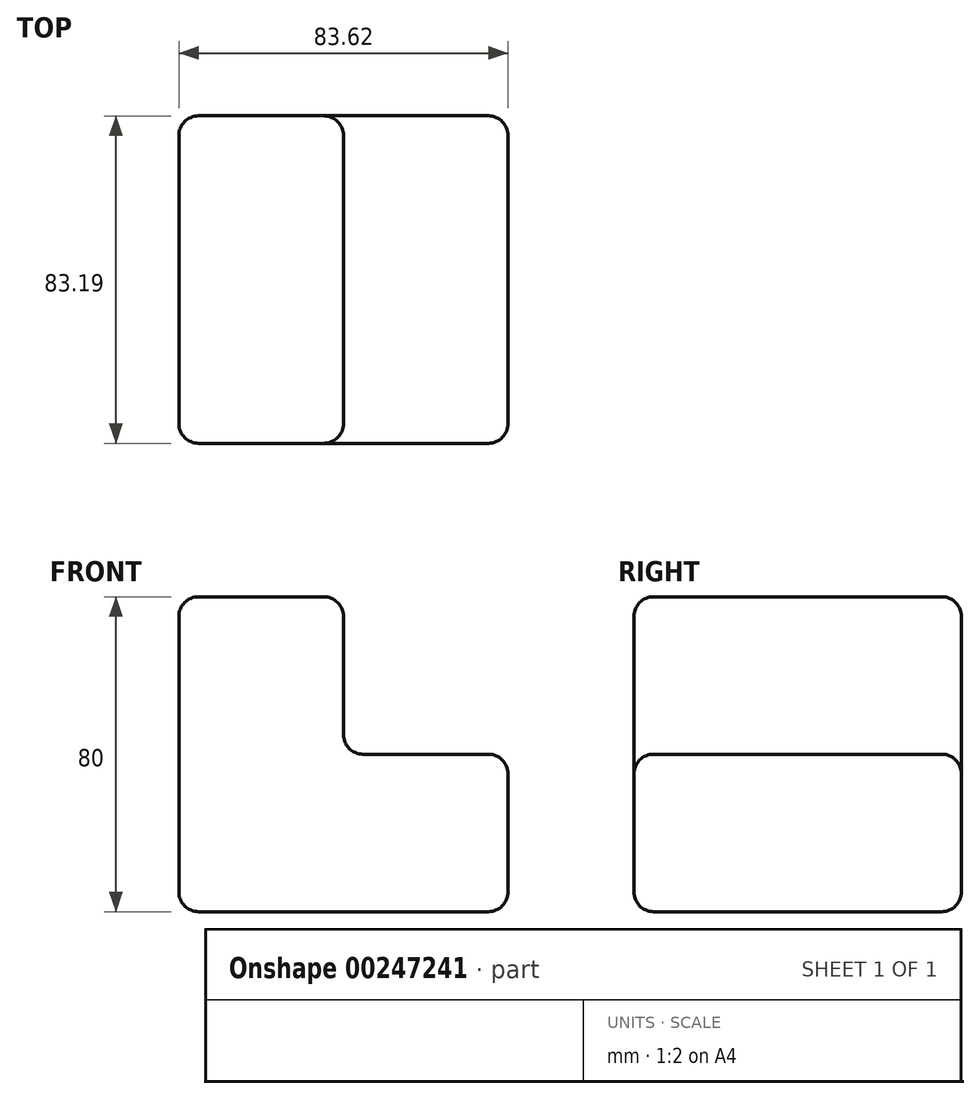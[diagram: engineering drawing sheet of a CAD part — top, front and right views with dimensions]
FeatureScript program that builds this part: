
annotation { "Feature Type Name" : "Feature", "Feature Type Description" : "" }
export const myFeature = defineFeature(function(context is Context, id is Id, definition is map)
    precondition{}
    {
        {
            var Q0;
            Q0=qCreatedBy(makeId("Top.planeOp"),FACE);
            var sketch = newSketch(context, id + "F0", { "sketchPlane" : qUnion([Q0])});
            skLineSegment(sketch, "E0.bottom", {"start": v(-59.13, -45.93) * mm, "end": v(24.5, -45.93) * mm});
            skLineSegment(sketch, "E0.top", {"start": v(-59.13, 37.26) * mm, "end": v(24.5, 37.26) * mm});
            skLineSegment(sketch, "E0.left", {"start": v(-59.13, -45.93) * mm, "end": v(-59.13, 37.26) * mm});
            skLineSegment(sketch, "E0.right", {"start": v(24.5, -45.93) * mm, "end": v(24.5, 37.26) * mm});
            skSolve(sketch);
        }
        {
            var Q0;
            Q0=makeQuery(id+"F0.imprint","IMPRINT",FACE,{"disambiguationData":[TD([[makeQuery(id+"F0.imprint","IMPRINT",EDGE,{"derivedFrom":sQuery(id+"F0.wireOp",EDGE,"E0.bottom")}),1.0]])]});
            extrude(context, id + "F1", {"entities" : qUnion([Q0]), "depth" : 40 * mm});
        }
        {
            var Q0;
            Q0=makeQuery(id+"F1.opExtrude","CAP_FACE",FACE,{"disambiguationData":[OSD([sQuery(id+"F0.wireOp",EDGE,"E0.bottom"),sQuery(id+"F0.wireOp",EDGE,"E0.top"),sQuery(id+"F0.wireOp",EDGE,"E0.left"),sQuery(id+"F0.wireOp",EDGE,"E0.right")])],"isStart":false});
            var sketch = newSketch(context, id + "F2", { "sketchPlane" : qUnion([Q0])});
            skLineSegment(sketch, "E1", {"start": v(-17.32, 37.26) * mm, "end": v(-17.32, -45.93) * mm});
            skSolve(sketch);
        }
        {
            var Q0;
            {var subQ1=sQuery(id+"F2.wireOp",EDGE,"E1");Q0=makeQuery(id+"F2.imprint","IMPRINT",FACE,{"disambiguationData":[TD([[makeQuery(id+"F2.imprint","IMPRINT",EDGE,{"derivedFrom":subQ1}),-1.0]])]});}
            extrude(context, id + "F3", {"entities" : qUnion([Q0]), "operationType" : NewBodyOperationType.ADD, "depth" : 40 * mm});
        }
        {
            var Q0;
            Q0=makeQuery(id+"F3.opExtrude","CAP_EDGE",EDGE,{"disambiguationData":[OSD([sQuery(id+"F2.wireOp",EDGE,"E1")])],"isStart":true});
            var Q1;
            {var subQ0=sQuery(id+"F0.wireOp",EDGE,"E0.left");Q1=makeQuery(id+"F3.boolean.opBoolean","MERGE",FACE,{"derivedFrom":[makeQuery(id+"F1.opExtrude","SWEPT_FACE",FACE,{"disambiguationData":[OSD([subQ0])]}),makeQuery(id+"F3.opExtrude","SWEPT_FACE",FACE,{"disambiguationData":[OSD([subQ0])]})]});}
            var Q2;
            Q2=makeQuery(id+"F1.opExtrude","CAP_EDGE",EDGE,{"disambiguationData":[OSD([sQuery(id+"F0.wireOp",EDGE,"E0.top")])],"isStart":false});
            var Q3;
            Q3=makeQuery(id+"F1.opExtrude","CAP_EDGE",EDGE,{"disambiguationData":[OSD([sQuery(id+"F0.wireOp",EDGE,"E0.bottom")])],"isStart":false});
            var Q4;
            {var subQ0=sQuery(id+"F0.wireOp",EDGE,"E0.top");Q4=makeQuery(id+"F3.boolean.opBoolean","MERGE",FACE,{"derivedFrom":[makeQuery(id+"F1.opExtrude","SWEPT_FACE",FACE,{"disambiguationData":[OSD([subQ0])]}),makeQuery(id+"F3.opExtrude","SWEPT_FACE",FACE,{"disambiguationData":[OSD([subQ0])]})]});}
            var Q5;
            Q5=makeQuery(id+"F3.opExtrude","CAP_EDGE",EDGE,{"disambiguationData":[OSD([sQuery(id+"F0.wireOp",EDGE,"E0.top")])],"isStart":false});
            var Q6;
            Q6=makeQuery(id+"F3.opExtrude","SWEPT_EDGE",EDGE,{"disambiguationData":[OSD([sQuery(id+"F0.wireOp",EDGE,"E0.bottom"),sQuery(id+"F2.wireOp",EDGE,"E1")])]});
            var Q7;
            Q7=makeQuery(id+"F1.opExtrude","CAP_FACE",FACE,{"disambiguationData":[OSD([sQuery(id+"F0.wireOp",EDGE,"E0.bottom"),sQuery(id+"F0.wireOp",EDGE,"E0.top"),sQuery(id+"F0.wireOp",EDGE,"E0.left"),sQuery(id+"F0.wireOp",EDGE,"E0.right")])],"isStart":true});
            var Q8;
            Q8=makeQuery(id+"F1.opExtrude","CAP_EDGE",EDGE,{"disambiguationData":[OSD([sQuery(id+"F0.wireOp",EDGE,"E0.right")])],"isStart":true});
            var Q9;
            Q9=makeQuery(id+"F1.opExtrude","CAP_EDGE",EDGE,{"disambiguationData":[OSD([sQuery(id+"F0.wireOp",EDGE,"E0.right")])],"isStart":false});
            var Q10;
            {var subQ0=sQuery(id+"F0.wireOp",EDGE,"E0.left");var subQ1=sQuery(id+"F0.wireOp",EDGE,"E0.bottom");Q10=makeQuery(id+"F3.boolean.opBoolean","MERGE",EDGE,{"derivedFrom":[makeQuery(id+"F1.opExtrude","SWEPT_EDGE",EDGE,{"disambiguationData":[OSD([subQ1,subQ0])]}),makeQuery(id+"F3.opExtrude","SWEPT_EDGE",EDGE,{"disambiguationData":[OSD([subQ1,subQ0])]})]});}
            var Q11;
            Q11=makeQuery(id+"F3.opExtrude","CAP_FACE",FACE,{"disambiguationData":[OSD([sQuery(id+"F0.wireOp",EDGE,"E0.bottom"),sQuery(id+"F0.wireOp",EDGE,"E0.top"),sQuery(id+"F0.wireOp",EDGE,"E0.left"),sQuery(id+"F2.wireOp",EDGE,"E1")])],"isStart":false});
            var Q12;
            Q12=makeQuery(id+"F3.opExtrude","SWEPT_FACE",FACE,{"disambiguationData":[OSD([sQuery(id+"F2.wireOp",EDGE,"E1")])]});
            var Q13;
            Q13=makeQuery(id+"F1.opExtrude","CAP_EDGE",EDGE,{"disambiguationData":[OSD([sQuery(id+"F0.wireOp",EDGE,"E0.bottom")])],"isStart":true});
            var Q14;
            Q14=makeQuery(id+"F1.opExtrude","SWEPT_FACE",FACE,{"disambiguationData":[OSD([sQuery(id+"F0.wireOp",EDGE,"E0.right")])]});
            var Q15;
            Q15=makeQuery(id+"F3.opExtrude","CAP_EDGE",EDGE,{"disambiguationData":[OSD([sQuery(id+"F2.wireOp",EDGE,"E1")])],"isStart":false});
            var Q16;
            Q16=makeQuery(id+"F3.opExtrude","CAP_EDGE",EDGE,{"disambiguationData":[OSD([sQuery(id+"F0.wireOp",EDGE,"E0.left")])],"isStart":false});
            var Q17;
            Q17=makeQuery(id+"F3.opExtrude","CAP_EDGE",EDGE,{"disambiguationData":[OSD([sQuery(id+"F0.wireOp",EDGE,"E0.bottom")])],"isStart":false});
            var Q18;
            {var subQ0=sQuery(id+"F0.wireOp",EDGE,"E0.bottom");Q18=makeQuery(id+"F3.boolean.opBoolean","MERGE",FACE,{"derivedFrom":[makeQuery(id+"F1.opExtrude","SWEPT_FACE",FACE,{"disambiguationData":[OSD([subQ0])]}),makeQuery(id+"F3.opExtrude","SWEPT_FACE",FACE,{"disambiguationData":[OSD([subQ0])]})]});}
            var Q19;
            Q19=makeQuery(id+"F3.opExtrude","SWEPT_EDGE",EDGE,{"disambiguationData":[OSD([sQuery(id+"F0.wireOp",EDGE,"E0.top"),sQuery(id+"F2.wireOp",EDGE,"E1")])]});
            var Q20;
            Q20=makeQuery(id+"F1.opExtrude","CAP_FACE",FACE,{"disambiguationData":[OSD([sQuery(id+"F0.wireOp",EDGE,"E0.bottom"),sQuery(id+"F0.wireOp",EDGE,"E0.top"),sQuery(id+"F0.wireOp",EDGE,"E0.left"),sQuery(id+"F0.wireOp",EDGE,"E0.right")])],"isStart":false});
            var Q21;
            {var subQ0=sQuery(id+"F0.wireOp",EDGE,"E0.left");var subQ1=sQuery(id+"F0.wireOp",EDGE,"E0.top");Q21=makeQuery(id+"F3.boolean.opBoolean","MERGE",EDGE,{"derivedFrom":[makeQuery(id+"F1.opExtrude","SWEPT_EDGE",EDGE,{"disambiguationData":[OSD([subQ1,subQ0])]}),makeQuery(id+"F3.opExtrude","SWEPT_EDGE",EDGE,{"disambiguationData":[OSD([subQ1,subQ0])]})]});}
            var Q22;
            Q22=makeQuery(id+"F1.opExtrude","CAP_EDGE",EDGE,{"disambiguationData":[OSD([sQuery(id+"F0.wireOp",EDGE,"E0.top")])],"isStart":true});
            var Q23;
            Q23=makeQuery(id+"F1.opExtrude","SWEPT_EDGE",EDGE,{"disambiguationData":[OSD([sQuery(id+"F0.wireOp",EDGE,"E0.top"),sQuery(id+"F0.wireOp",EDGE,"E0.right")])]});
            var Q24;
            Q24=makeQuery(id+"F1.opExtrude","CAP_EDGE",EDGE,{"disambiguationData":[OSD([sQuery(id+"F0.wireOp",EDGE,"E0.left")])],"isStart":true});
            var Q25;
            Q25=makeQuery(id+"F1.opExtrude","SWEPT_EDGE",EDGE,{"disambiguationData":[OSD([sQuery(id+"F0.wireOp",EDGE,"E0.bottom"),sQuery(id+"F0.wireOp",EDGE,"E0.right")])]});
            fillet(context, id + "F4", {"entities" : qUnion([Q0, Q1, Q2, Q3, Q4, Q5, Q6, Q7, Q8, Q9, Q10, Q11, Q12, Q13, Q14, Q15, Q16, Q17, Q18, Q19, Q20, Q21, Q22, Q23, Q24, Q25]), "radius" : 5 * mm, "tangentPropagation" : true, "allowEdgeOverflow" : false});
        }
    });
